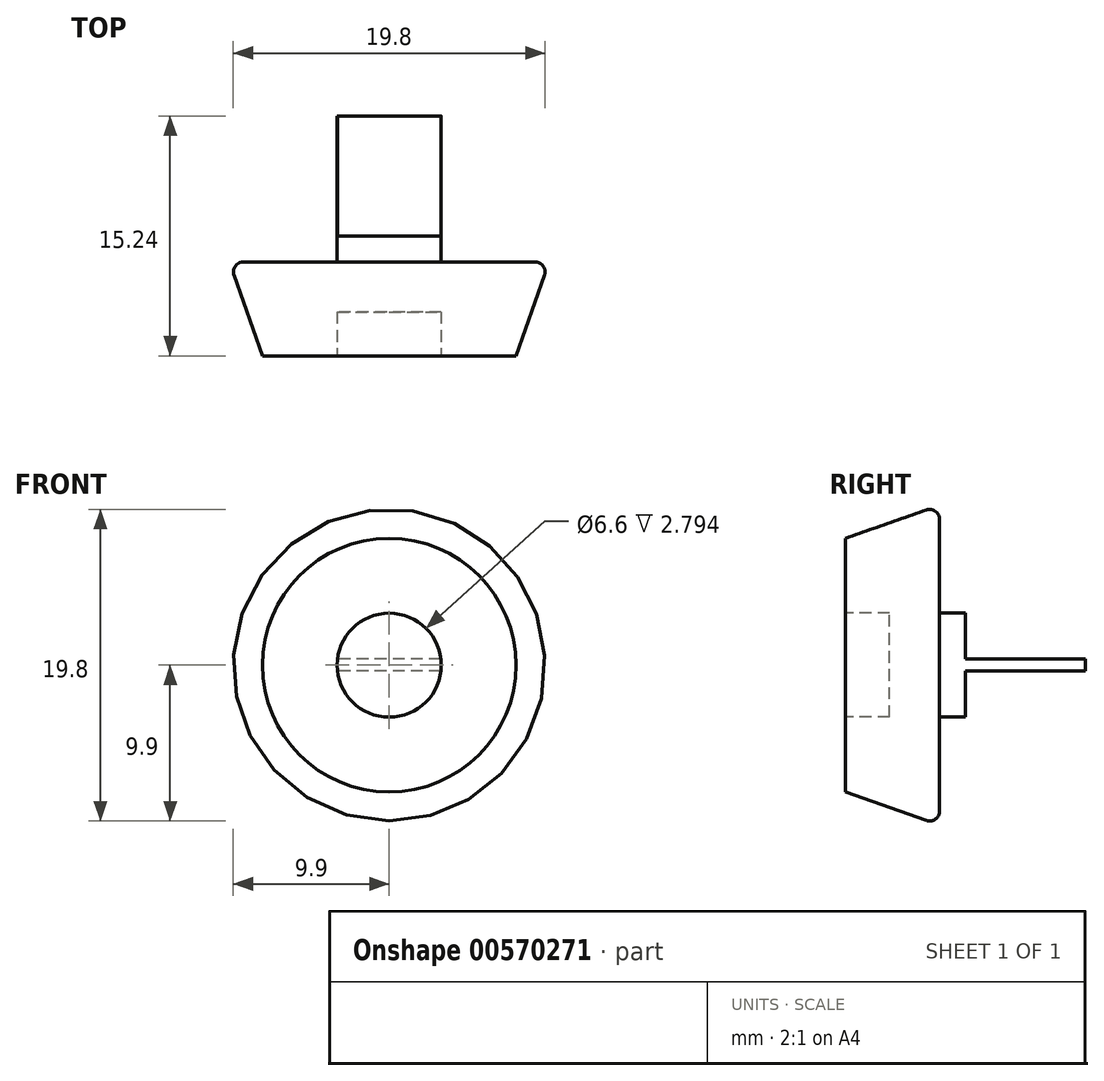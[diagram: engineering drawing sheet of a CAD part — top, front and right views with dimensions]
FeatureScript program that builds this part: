
annotation { "Feature Type Name" : "Feature", "Feature Type Description" : "" }
export const myFeature = defineFeature(function(context is Context, id is Id, definition is map)
    precondition{}
    {
        {
            var Q0;
            Q0=qCreatedBy(makeId("Top.planeOp"),FACE);
            var sketch = newSketch(context, id + "F0", { "sketchPlane" : qUnion([Q0])});
            skLineSegment(sketch, "E0", {"start": v(0, 0) * mm, "end": v(0, 7.62) * mm});
            skLineSegment(sketch, "E1", {"start": v(0, 7.62) * mm, "end": v(0, 10.8) * mm});
            skLineSegment(sketch, "E2", {"start": v(0, 10.8) * mm, "end": v(0, 17.14) * mm});
            skLineSegment(sketch, "E3", {"start": v(0, 17.14) * mm, "end": v(0, 29.85) * mm});
            skLineSegment(sketch, "E4", {"start": v(0, 29.85) * mm, "end": v(4.7, 29.85) * mm});
            skLineSegment(sketch, "E5", {"start": v(0, 17.14) * mm, "end": v(2.16, 17.14) * mm});
            skLineSegment(sketch, "E6", {"start": v(0, 10.8) * mm, "end": v(10.16, 10.8) * mm});
            skLineSegment(sketch, "E7", {"start": v(0, 7.62) * mm, "end": v(3.3, 7.62) * mm});
            skLineSegment(sketch, "E8", {"start": v(0, 0) * mm, "end": v(6.35, 0) * mm});
            skLineSegment(sketch, "E9", {"start": v(6.35, 0) * mm, "end": v(10.16, 10.8) * mm});
            skLineSegment(sketch, "E10", {"start": v(4.7, 29.85) * mm, "end": v(4.7, 10.8) * mm});
            skLineSegment(sketch, "E11", {"start": v(2.16, 17.14) * mm, "end": v(2.16, 29.85) * mm});
            skLineSegment(sketch, "E12", {"start": v(3.3, 7.62) * mm, "end": v(3.3, 0) * mm});
            skLineSegment(sketch, "E13", {"start": v(0, 0) * mm, "end": v(0, 4.83) * mm});
            skLineSegment(sketch, "E14", {"start": v(0, 4.83) * mm, "end": v(8.05, 4.83) * mm});
            skLineSegment(sketch, "E15", {"start": v(0, 4.83) * mm, "end": v(0, 12.45) * mm});
            skLineSegment(sketch, "E16", {"start": v(0, 12.45) * mm, "end": v(3.3, 12.45) * mm});
            skLineSegment(sketch, "E17", {"start": v(3.3, 12.45) * mm, "end": v(3.3, 7.62) * mm});
            skSolve(sketch);
        }
        {
            var Q0;
            {var subQ4=sQuery(id+"F0.wireOp",EDGE,"E2");Q0=makeQuery(id+"F0.imprint","IMPRINT",FACE,{"disambiguationData":[TD([[makeQuery(id+"F0.imprint","IMPRINT",EDGE,{"derivedFrom":subQ4}),-1.0]])]});}
            var Q1;
            {var subQ3=sQuery(id+"F0.wireOp",EDGE,"E1");Q1=makeQuery(id+"F0.imprint","IMPRINT",FACE,{"disambiguationData":[TD([[makeQuery(id+"F0.imprint","IMPRINT",EDGE,{"derivedFrom":subQ3}),-1.0]])]});}
            var Q2;
            {var subQ6=sQuery(id+"F0.wireOp",EDGE,"E6");var subQ9=makeQuery(id+"F0.imprint","INTERSECT",VERTEX,{"derivedFrom":[subQ6,sQuery(id+"F0.wireOp",EDGE,"E10")]});Q2=makeQuery(id+"F0.imprint","IMPRINT",FACE,{"disambiguationData":[TD([[makeQuery(id+"F0.imprint","IMPRINT",EDGE,{"disambiguationData":[TD([[subQ9,1.0]])],"derivedFrom":subQ6}),-1.0]])]});}
            var Q3;
            Q3=sQuery(id+"F0.wireOp",EDGE,"E3");
            revolve(context, id + "F1", {"entities" : qUnion([Q0, Q1, Q2]), "axis" : qUnion([Q3]), "revolveType" : RevolveType.FULL, "surfaceOperationType" : NewSurfaceOperationType.NEW});
        }
        {
            var Q0;
            Q0=makeQuery(id+"F1.opRevolve","SWEPT_FACE",FACE,{"disambiguationData":[OSD([sQuery(id+"F0.wireOp",EDGE,"E16")])]});
            var sketch = newSketch(context, id + "F2", { "sketchPlane" : qUnion([Q0])});
            skLineSegment(sketch, "E18.bottom", {"start": v(-3.56, -0.38) * mm, "end": v(3.56, -0.38) * mm});
            skLineSegment(sketch, "E18.top", {"start": v(-3.56, 0.38) * mm, "end": v(3.56, 0.38) * mm});
            skLineSegment(sketch, "E18.left", {"start": v(-3.56, -0.38) * mm, "end": v(-3.56, 0.38) * mm});
            skLineSegment(sketch, "E18.right", {"start": v(3.56, -0.38) * mm, "end": v(3.56, 0.38) * mm});
            skPoint(sketch, "E18.middle", {"position": v(0, 0) * mm});
            skSolve(sketch);
        }
        {
            var Q0;
            {var subQ0=sQuery(id+"F2.wireOp",EDGE,"E18.bottom");var subQ1=makeQuery(id+"F1.opRevolve","SWEPT_EDGE",EDGE,{"disambiguationData":[OSD([sQuery(id+"F0.wireOp",EDGE,"E7"),sQuery(id+"F0.wireOp",EDGE,"E12")])]});var subQ2=makeQuery(id+"F2.imprint","INTERSECT",VERTEX,{"disambiguationData":[OD(0.0)],"derivedFrom":[subQ1,subQ0]});Q0=makeQuery(id+"F2.imprint","IMPRINT",FACE,{"disambiguationData":[TD([[makeQuery(id+"F2.imprint","IMPRINT",EDGE,{"disambiguationData":[TD([[subQ2,-1.0]])],"derivedFrom":subQ0}),1.0]])]});}
            var Q1;
            {var subQ0=sQuery(id+"F2.wireOp",EDGE,"E18.bottom");var subQ1=makeQuery(id+"F1.opRevolve","SWEPT_EDGE",EDGE,{"disambiguationData":[OSD([sQuery(id+"F0.wireOp",EDGE,"E16"),sQuery(id+"F0.wireOp",EDGE,"E17")])]});var subQ2=makeQuery(id+"F2.imprint","INTERSECT",VERTEX,{"disambiguationData":[OD(0.0)],"derivedFrom":[subQ1,subQ0]});Q1=makeQuery(id+"F2.imprint","IMPRINT",FACE,{"disambiguationData":[TD([[makeQuery(id+"F2.imprint","IMPRINT",EDGE,{"disambiguationData":[TD([[subQ2,-1.0]])],"derivedFrom":subQ0}),1.0]])]});}
            extrude(context, id + "F3", {"entities" : qUnion([Q0, Q1]), "operationType" : NewBodyOperationType.ADD, "depth" : 7.62 * mm, "offsetDistance" : 25.4 * mm});
        }
        {
            var Q0;
            Q0=makeQuery(id+"F1.opRevolve","SWEPT_EDGE",EDGE,{"disambiguationData":[OSD([sQuery(id+"F0.wireOp",EDGE,"E6"),sQuery(id+"F0.wireOp",EDGE,"E9")])]});
            fillet(context, id + "F4", {"entities" : qUnion([Q0]), "radius" : 0.64 * mm, "tangentPropagation" : true, "allowEdgeOverflow" : false});
        }
    });
